# Revit family: ACU-Medium Opera Pendant
name_source: partatom
category: Lighting Fixtures
units: mm (PartAtom-declared; Revit-internal decimal feet)

## family parameters
Always vertical = Yes
Cut with Voids When Loaded = No
Host = Ceiling
Light Source = Yes
OmniClass Number = 23.80.70.11
OmniClass Title = Luminaries for Internal Lighting
Part Type = Normal
Room Calculation Point = No
Round Connector Dimension = Use Diameter
Shared = No

## types (1)
- Type 1
    Bracket Material = Acustico - Stainless Steel
    Cable Material = Acustico - Timber
    Color Filter = 16777215
    Default Elevation = 0 mm  [stored 0 ft]
    Description = 600mm Punk Pendant
    Dimming Lamp Color Temperature Shift = <None>
    Emit Shape Visible in Rendering = No
    Emit from Circle Diameter = 400 mm  [stored 1.31234 ft]
    Internal Pendant Material = Acustico - Rouge
    Light Source Material = Acustico - Perpsex
    Manufacturer = Acustico lighting
    Pendant Material = Acustico - Light Grey
    Photometric Web File = MED - 2500_CLE-ADV4-190-220mm (1).ies
    Plate Thickness = 3 mm  [stored 0.00984252 ft]
    Tilt Angle = 90.00°

note: [stored X ft] marks values corroborated as IEEE doubles in the binary element streams (Revit-internal decimal feet)

## geometry (parser evidence)
native form markers: Sweep x1
no freeform markers — native parametric forms only
